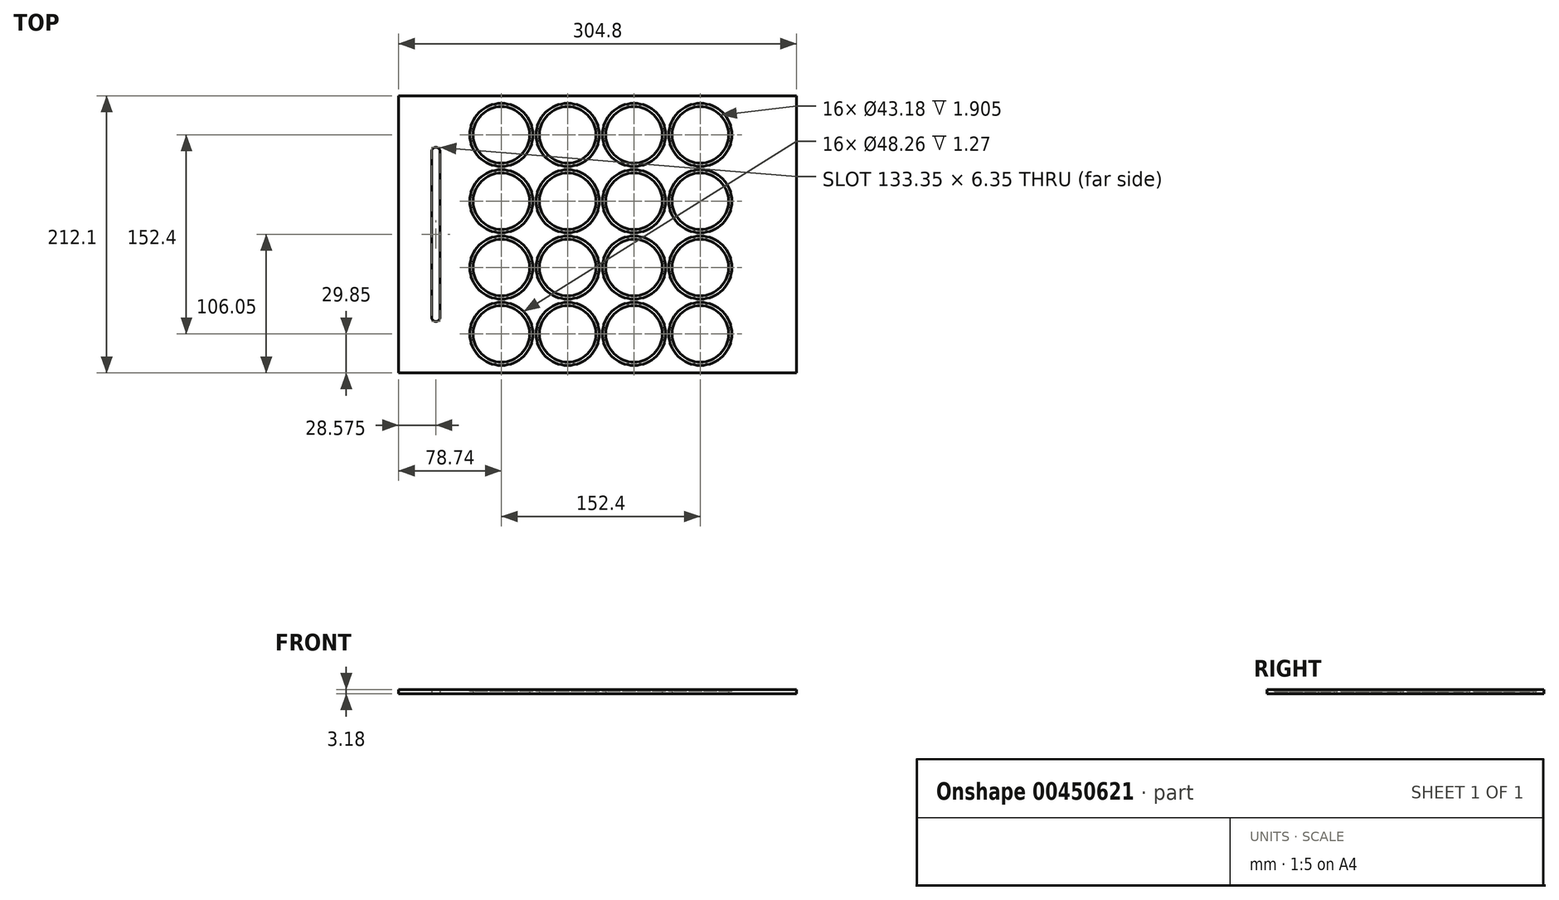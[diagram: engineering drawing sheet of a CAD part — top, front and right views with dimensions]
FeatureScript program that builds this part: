
annotation { "Feature Type Name" : "Feature", "Feature Type Description" : "" }
export const myFeature = defineFeature(function(context is Context, id is Id, definition is map)
    precondition{}
    {
        {
            var Q0;
            Q0=qCreatedBy(makeId("Top.planeOp"),FACE);
            var sketch = newSketch(context, id + "F0", { "sketchPlane" : qUnion([Q0])});
            skLineSegment(sketch, "E0.bottom", {"start": v(0, 106.05) * mm, "end": v(-304.8, 106.05) * mm});
            skLineSegment(sketch, "E0.top", {"start": v(0, -106.05) * mm, "end": v(-304.8, -106.05) * mm});
            skLineSegment(sketch, "E0.left", {"start": v(0, 106.05) * mm, "end": v(0, -106.05) * mm});
            skLineSegment(sketch, "E0.right", {"start": v(-304.8, 106.05) * mm, "end": v(-304.8, -106.05) * mm});
            skPoint(sketch, "E1", {"position": v(0, 0) * mm});
            skCircle(sketch, "E2", {"center": v(-226.06, 76.2) * mm, "radius": 21.59 * mm});
            skCircle(sketch, "E3.0.1.0", {"center": v(-226.06, 25.4) * mm, "radius": 21.59 * mm});
            skCircle(sketch, "E3.0.2.0", {"center": v(-226.06, -25.4) * mm, "radius": 21.59 * mm});
            skCircle(sketch, "E3.0.3.0", {"center": v(-226.06, -76.2) * mm, "radius": 21.59 * mm});
            skCircle(sketch, "E3.1.0.0", {"center": v(-175.26, 76.2) * mm, "radius": 21.59 * mm});
            skCircle(sketch, "E3.1.1.0", {"center": v(-175.26, 25.4) * mm, "radius": 21.59 * mm});
            skCircle(sketch, "E3.1.2.0", {"center": v(-175.26, -25.4) * mm, "radius": 21.59 * mm});
            skCircle(sketch, "E3.1.3.0", {"center": v(-175.26, -76.2) * mm, "radius": 21.59 * mm});
            skCircle(sketch, "E3.2.0.0", {"center": v(-124.46, 76.2) * mm, "radius": 21.59 * mm});
            skCircle(sketch, "E3.2.1.0", {"center": v(-124.46, 25.4) * mm, "radius": 21.59 * mm});
            skCircle(sketch, "E3.2.2.0", {"center": v(-124.46, -25.4) * mm, "radius": 21.59 * mm});
            skCircle(sketch, "E3.2.3.0", {"center": v(-124.46, -76.2) * mm, "radius": 21.59 * mm});
            skCircle(sketch, "E3.3.0.0", {"center": v(-73.66, 76.2) * mm, "radius": 21.59 * mm});
            skCircle(sketch, "E3.3.1.0", {"center": v(-73.66, 25.4) * mm, "radius": 21.59 * mm});
            skCircle(sketch, "E3.3.2.0", {"center": v(-73.66, -25.4) * mm, "radius": 21.59 * mm});
            skCircle(sketch, "E3.3.3.0", {"center": v(-73.66, -76.2) * mm, "radius": 21.59 * mm});
            skLineSegment(sketch, "E3.direction1", {"start": v(-226.06, 76.2) * mm, "end": v(-175.26, 76.2) * mm, "construction": true});
            skLineSegment(sketch, "E3.direction2", {"start": v(-226.06, 76.2) * mm, "end": v(-226.06, 25.4) * mm, "construction": true});
            skLineSegment(sketch, "E4", {"start": v(-175.26, 25.4) * mm, "end": v(-175.26, -25.4) * mm, "construction": true});
            skLineSegment(sketch, "E5", {"start": v(0, 0) * mm, "end": v(-175.26, 0) * mm, "construction": true});
            skPoint(sketch, "E6", {"position": v(-175.26, 0) * mm});
            skLineSegment(sketch, "E7", {"start": v(-304.8, 0) * mm, "end": v(-276.23, 0) * mm, "construction": true});
            skLineSegment(sketch, "E8.left", {"start": v(-273.05, 63.5) * mm, "end": v(-273.05, -63.5) * mm});
            skLineSegment(sketch, "E8.right", {"start": v(-279.4, 63.5) * mm, "end": v(-279.4, -63.5) * mm});
            skPoint(sketch, "E8.middle", {"position": v(-276.23, 0) * mm});
            skArc(sketch, "E9", {"start": v(-273.05, 63.5) * mm, "mid": v(-276.23, 66.68) * mm, "end": v(-279.4, 63.5) * mm});
            skArc(sketch, "E10", {"start": v(-279.4, -63.5) * mm, "mid": v(-276.23, -66.68) * mm, "end": v(-273.05, -63.5) * mm});
            skSolve(sketch);
        }
        {
            var Q0;
            Q0 = qSketchRegion(id + "F0", true);
            extrude(context, id + "F1", {"entities" : qUnion([Q0]), "depth" : 3.17 * mm});
        }
        {
            var Q0;
            Q0=makeQuery(id+"F1.opExtrude","CAP_FACE",FACE,{"disambiguationData":[OSD([sQuery(id+"F0.wireOp",EDGE,"E0.bottom"),sQuery(id+"F0.wireOp",EDGE,"E0.top"),sQuery(id+"F0.wireOp",EDGE,"E0.left"),sQuery(id+"F0.wireOp",EDGE,"E0.right"),sQuery(id+"F0.wireOp",EDGE,"E2"),sQuery(id+"F0.wireOp",EDGE,"E3.0.1.0"),sQuery(id+"F0.wireOp",EDGE,"E3.0.2.0"),sQuery(id+"F0.wireOp",EDGE,"E3.0.3.0"),sQuery(id+"F0.wireOp",EDGE,"E3.1.0.0"),sQuery(id+"F0.wireOp",EDGE,"E3.1.1.0"),sQuery(id+"F0.wireOp",EDGE,"E3.1.2.0"),sQuery(id+"F0.wireOp",EDGE,"E3.1.3.0"),sQuery(id+"F0.wireOp",EDGE,"E3.2.0.0"),sQuery(id+"F0.wireOp",EDGE,"E3.2.1.0"),sQuery(id+"F0.wireOp",EDGE,"E3.2.2.0"),sQuery(id+"F0.wireOp",EDGE,"E3.2.3.0"),sQuery(id+"F0.wireOp",EDGE,"E3.3.0.0"),sQuery(id+"F0.wireOp",EDGE,"E3.3.1.0"),sQuery(id+"F0.wireOp",EDGE,"E3.3.2.0"),sQuery(id+"F0.wireOp",EDGE,"E3.3.3.0"),sQuery(id+"F0.wireOp",EDGE,"E8.left"),sQuery(id+"F0.wireOp",EDGE,"E8.right"),sQuery(id+"F0.wireOp",EDGE,"E9"),sQuery(id+"F0.wireOp",EDGE,"E10")])],"isStart":false});
            var sketch = newSketch(context, id + "F2", { "sketchPlane" : qUnion([Q0])});
            skCircle(sketch, "E11.0", {"center": v(-226.06, 76.2) * mm, "radius": 24.13 * mm});
            skCircle(sketch, "E12.0.1.0", {"center": v(-226.06, 25.4) * mm, "radius": 24.13 * mm});
            skCircle(sketch, "E12.0.2.0", {"center": v(-226.06, -25.4) * mm, "radius": 24.13 * mm});
            skCircle(sketch, "E12.0.3.0", {"center": v(-226.06, -76.2) * mm, "radius": 24.13 * mm});
            skCircle(sketch, "E12.1.0.0", {"center": v(-175.26, 76.2) * mm, "radius": 24.13 * mm});
            skCircle(sketch, "E12.1.1.0", {"center": v(-175.26, 25.4) * mm, "radius": 24.13 * mm});
            skCircle(sketch, "E12.1.2.0", {"center": v(-175.26, -25.4) * mm, "radius": 24.13 * mm});
            skCircle(sketch, "E12.1.3.0", {"center": v(-175.26, -76.2) * mm, "radius": 24.13 * mm});
            skCircle(sketch, "E12.2.0.0", {"center": v(-124.46, 76.2) * mm, "radius": 24.13 * mm});
            skCircle(sketch, "E12.2.1.0", {"center": v(-124.46, 25.4) * mm, "radius": 24.13 * mm});
            skCircle(sketch, "E12.2.2.0", {"center": v(-124.46, -25.4) * mm, "radius": 24.13 * mm});
            skCircle(sketch, "E12.2.3.0", {"center": v(-124.46, -76.2) * mm, "radius": 24.13 * mm});
            skCircle(sketch, "E12.3.0.0", {"center": v(-73.66, 76.2) * mm, "radius": 24.13 * mm});
            skCircle(sketch, "E12.3.1.0", {"center": v(-73.66, 25.4) * mm, "radius": 24.13 * mm});
            skCircle(sketch, "E12.3.2.0", {"center": v(-73.66, -25.4) * mm, "radius": 24.13 * mm});
            skCircle(sketch, "E12.3.3.0", {"center": v(-73.66, -76.2) * mm, "radius": 24.13 * mm});
            skLineSegment(sketch, "E12.direction1", {"start": v(-226.06, 76.2) * mm, "end": v(-175.26, 76.2) * mm, "construction": true});
            skLineSegment(sketch, "E12.direction2", {"start": v(-226.06, 76.2) * mm, "end": v(-226.06, 25.4) * mm, "construction": true});
            skSolve(sketch);
        }
        {
            var Q0;
            Q0 = qSketchRegion(id + "F2", true);
            extrude(context, id + "F3", {"entities" : qUnion([Q0]), "operationType" : NewBodyOperationType.REMOVE, "oppositeDirection" : true, "depth" : 1.27 * mm});
        }
    });
